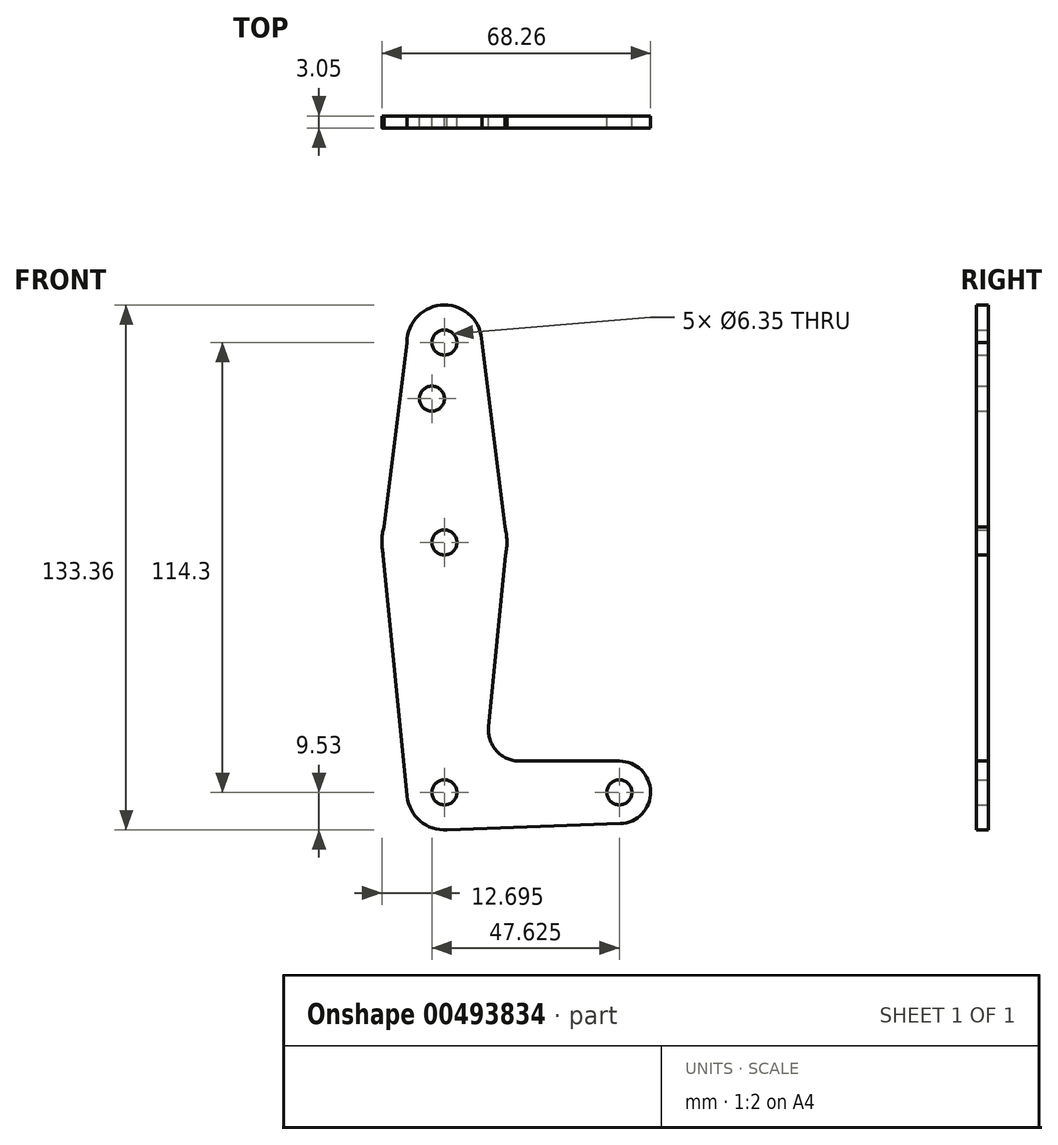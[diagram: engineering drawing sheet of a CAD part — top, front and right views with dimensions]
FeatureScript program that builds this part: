
annotation { "Feature Type Name" : "Feature", "Feature Type Description" : "" }
export const myFeature = defineFeature(function(context is Context, id is Id, definition is map)
    precondition{}
    {
        {
            var Q0;
            Q0=qCreatedBy(makeId("Front.planeOp"),FACE);
            var sketch = newSketch(context, id + "F0", { "sketchPlane" : qUnion([Q0])});
            skLineSegment(sketch, "E0", {"start": v(0, 0) * mm, "end": v(0, 114.3) * mm});
            skLineSegment(sketch, "E1", {"start": v(0, 0) * mm, "end": v(44.45, 0) * mm});
            skCircle(sketch, "E2", {"center": v(0, 114.3) * mm, "radius": 9.53 * mm});
            skCircle(sketch, "E3", {"center": v(0, 0) * mm, "radius": 9.53 * mm});
            skCircle(sketch, "E4", {"center": v(44.45, 0) * mm, "radius": 7.94 * mm});
            skCircle(sketch, "E5", {"center": v(0, 63.5) * mm, "radius": 15.88 * mm});
            skLineSegment(sketch, "E6", {"start": v(0, 114.3) * mm, "end": v(-9.53, 114.3) * mm});
            skLineSegment(sketch, "E7", {"start": v(-9.52, 114.3) * mm, "end": v(-15.88, 63.5) * mm});
            skLineSegment(sketch, "E8", {"start": v(0, 114.3) * mm, "end": v(9.53, 114.3) * mm});
            skLineSegment(sketch, "E9", {"start": v(9.52, 114.3) * mm, "end": v(15.88, 63.5) * mm});
            skLineSegment(sketch, "E10", {"start": v(0, 63.5) * mm, "end": v(-15.88, 63.5) * mm});
            skLineSegment(sketch, "E11", {"start": v(-15.88, 63.5) * mm, "end": v(-9.48, -0.94) * mm});
            skLineSegment(sketch, "E12", {"start": v(0, 63.5) * mm, "end": v(15.88, 63.5) * mm});
            skLineSegment(sketch, "E13", {"start": v(15.88, 63.5) * mm, "end": v(11.23, 16.67) * mm});
            skLineSegment(sketch, "E14", {"start": v(0, 0) * mm, "end": v(0, 9.53) * mm});
            skLineSegment(sketch, "E15", {"start": v(19.14, 7.94) * mm, "end": v(44.45, 7.94) * mm});
            skLineSegment(sketch, "E16", {"start": v(0, 0) * mm, "end": v(0, -9.53) * mm});
            skLineSegment(sketch, "E17", {"start": v(0, -9.53) * mm, "end": v(44.73, -7.93) * mm});
            skCircle(sketch, "E18", {"center": v(0, 114.3) * mm, "radius": 3.18 * mm});
            skCircle(sketch, "E19", {"center": v(-3.18, 100.03) * mm, "radius": 3.18 * mm});
            skCircle(sketch, "E20", {"center": v(0, 63.5) * mm, "radius": 3.18 * mm});
            skCircle(sketch, "E21", {"center": v(0, 0) * mm, "radius": 3.18 * mm});
            skCircle(sketch, "E22", {"center": v(44.45, 0) * mm, "radius": 3.18 * mm});
            skArc(sketch, "E23.filletArc", {"start": v(11.23, 16.67) * mm, "mid": v(13.25, 10.55) * mm, "end": v(19.14, 7.94) * mm});
            skSolve(sketch);
        }
        {
            var Q0;
            Q0 = qSketchRegion(id + "F0", true);
            var Q1;
            {var subQ0=sQuery(id+"F0.wireOp",EDGE,"E21");var subQ1=sQuery(id+"F0.wireOp",EDGE,"E1");var subQ2=makeQuery(id+"F0.imprint","INTERSECT",VERTEX,{"derivedFrom":[subQ1,subQ0]});Q1=makeQuery(id+"F0.imprint","IMPRINT",FACE,{"disambiguationData":[TD([[makeQuery(id+"F0.imprint","IMPRINT",EDGE,{"disambiguationData":[TD([[subQ2,-1.0]])],"derivedFrom":subQ1}),1.0]])]});}
            extrude(context, id + "F1", {"entities" : qUnion([Q0, Q1]), "depth" : 3.05 * mm});
        }
    });
